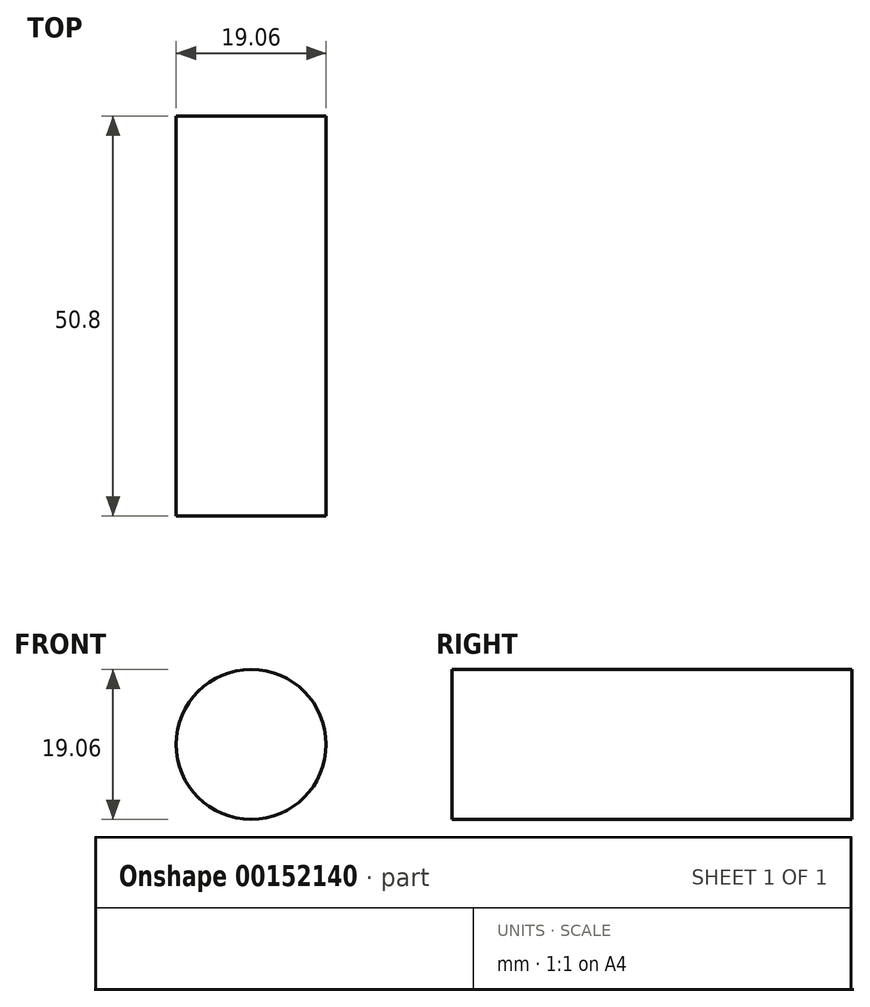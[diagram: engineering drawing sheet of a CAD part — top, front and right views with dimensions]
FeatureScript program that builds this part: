
annotation { "Feature Type Name" : "Feature", "Feature Type Description" : "" }
export const myFeature = defineFeature(function(context is Context, id is Id, definition is map)
    precondition{}
    {
        {
            var Q0;
            Q0=qCreatedBy(makeId("Front.planeOp"),FACE);
            var sketch = newSketch(context, id + "F0", { "sketchPlane" : qUnion([Q0])});
            skCircle(sketch, "E0", {"center": v(0, 0) * mm, "radius": 9.53 * mm});
            skSolve(sketch);
        }
        {
            var Q0;
            Q0 = qSketchRegion(id + "F0", true);
            extrude(context, id + "F1", {"entities" : qUnion([Q0]), "depth" : 50.8 * mm});
        }
    });
